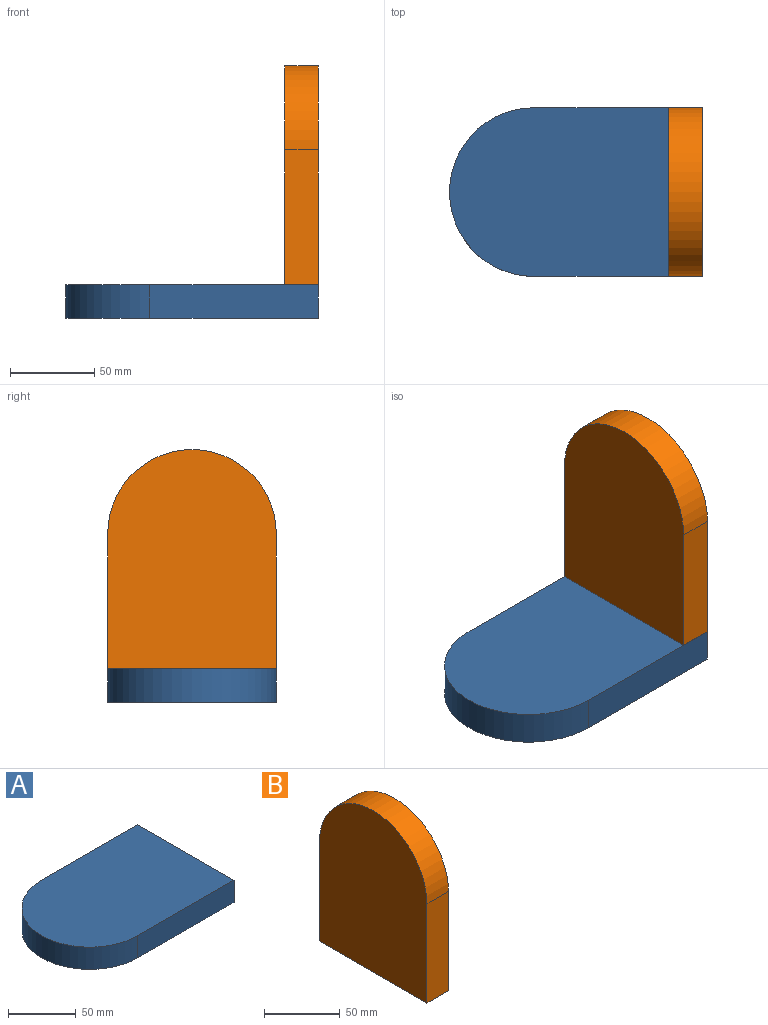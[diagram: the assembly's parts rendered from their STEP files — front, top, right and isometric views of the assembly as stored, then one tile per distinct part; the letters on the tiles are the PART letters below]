
ASSEMBLY  parts=2 mates=1
PART A: 6 faces, bbox 150x100x20 mm
  f0: plane 100x20mm, normal (0,1,0), area 2000mm2, adj f1,f3,f4,f5
  f1: cylinder r=50mm len=100mm, axis (0,0,-1), area 3141.6mm2, adj f0,f2,f4,f5
  f2: plane 100x20mm, normal (0,-1,0), area 2000mm2, adj f1,f3,f4,f5
  f3: plane 100x20mm, normal (1,0,0), area 2000mm2, adj f0,f2,f4,f5
  f4: plane 150x100mm, normal (0,0,1), area 13927mm2, adj f0,f1,f2,f3
  f5: plane 150x100mm, normal (0,0,-1), area 13927mm2, adj f0,f1,f2,f3
PART B: 6 faces, bbox 20x100x130 mm
  f0: plane 80x20mm, normal (0,1,0), area 1600mm2, adj f1,f3,f4,f5
  f1: cylinder r=50mm len=100mm, axis (-1,0,0), area 3141.6mm2, adj f0,f2,f4,f5
  f2: plane 80x20mm, normal (0,-1,0), area 1600mm2, adj f1,f3,f4,f5
  f3: plane 100x20mm, normal (0,0,-1), area 2000mm2, adj f0,f2,f4,f5
  f4: plane 130x100mm, normal (1,0,0), area 11927mm2, adj f0,f1,f2,f3
  f5: plane 130x100mm, normal (-1,0,0), area 11927mm2, adj f0,f1,f2,f3
PLACE A t=(-132.5,51.47,10.06)mm
PLACE B t=(-52.5,51.47,110.06)mm
MATE fastened A.f4 <-> B.f3  axis (0,0,1) through (-32.5,1.47,30.06)mm
